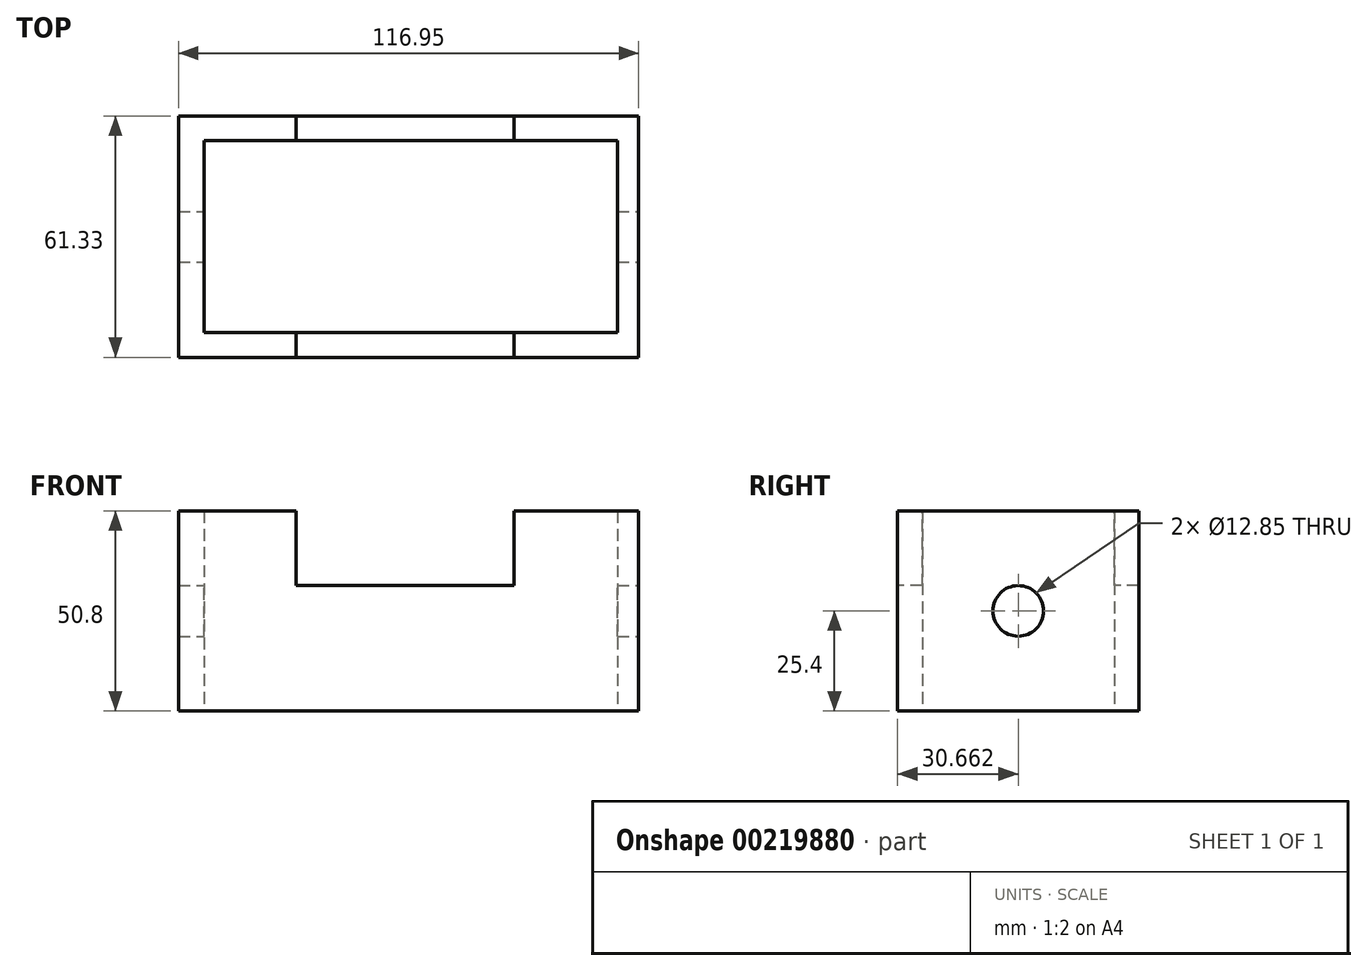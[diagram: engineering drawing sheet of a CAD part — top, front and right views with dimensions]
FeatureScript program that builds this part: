
annotation { "Feature Type Name" : "Feature", "Feature Type Description" : "" }
export const myFeature = defineFeature(function(context is Context, id is Id, definition is map)
    precondition{}
    {
        {
            var Q0;
            Q0=qCreatedBy(makeId("Top.planeOp"),FACE);
            var sketch = newSketch(context, id + "F0", { "sketchPlane" : qUnion([Q0])});
            skLineSegment(sketch, "E0.bottom", {"start": v(-55.34, 27.53) * mm, "end": v(61.61, 27.53) * mm});
            skLineSegment(sketch, "E0.top", {"start": v(-55.34, -33.8) * mm, "end": v(61.61, -33.8) * mm});
            skLineSegment(sketch, "E0.left", {"start": v(-55.34, 27.53) * mm, "end": v(-55.34, -33.8) * mm});
            skLineSegment(sketch, "E0.right", {"start": v(61.61, 27.53) * mm, "end": v(61.61, -33.8) * mm});
            skLineSegment(sketch, "E1.bottom", {"start": v(-48.78, 21.25) * mm, "end": v(56.2, 21.25) * mm});
            skLineSegment(sketch, "E1.top", {"start": v(-48.78, -27.53) * mm, "end": v(56.2, -27.53) * mm});
            skLineSegment(sketch, "E1.left", {"start": v(-48.78, 21.25) * mm, "end": v(-48.78, -27.53) * mm});
            skLineSegment(sketch, "E1.right", {"start": v(56.2, 21.25) * mm, "end": v(56.2, -27.53) * mm});
            skSolve(sketch);
        }
        {
            var Q0;
            Q0 = qSketchRegion(id + "F0", true);
            extrude(context, id + "F1", {"entities" : qUnion([Q0]), "depth" : 50.8 * mm});
        }
        {
            var Q0;
            Q0=makeQuery(id+"F1.opExtrude","SWEPT_FACE",FACE,{"disambiguationData":[OSD([sQuery(id+"F0.wireOp",EDGE,"E0.top")])]});
            var sketch = newSketch(context, id + "F2", { "sketchPlane" : qUnion([Q0])});
            skLineSegment(sketch, "E2", {"start": v(-25.39, 50.8) * mm, "end": v(-25.39, 31.8) * mm});
            skLineSegment(sketch, "E3", {"start": v(-25.39, 31.8) * mm, "end": v(29.95, 31.8) * mm});
            skLineSegment(sketch, "E4", {"start": v(29.95, 31.8) * mm, "end": v(29.95, 50.8) * mm});
            skSolve(sketch);
        }
        {
            var Q0;
            {var subQ0=sQuery(id+"F2.wireOp",EDGE,"E2");Q0=makeQuery(id+"F2.imprint","IMPRINT",FACE,{"disambiguationData":[TD([[makeQuery(id+"F2.imprint","IMPRINT",EDGE,{"derivedFrom":subQ0}),1.0]])]});}
            var Q1;
            Q1=sQuery(id+"F2.wireOp",EDGE,"E4");
            var Q2;
            Q2=sQuery(id+"F2.wireOp",EDGE,"E3");
            var Q3;
            Q3=sQuery(id+"F2.wireOp",EDGE,"E2");
            extrude(context, id + "F3", {"entities" : qUnion([Q0]), "operationType" : NewBodyOperationType.REMOVE, "surfaceEntities" : qUnion([Q1, Q2, Q3]), "oppositeDirection" : true, "depth" : 76.2 * mm});
        }
        {
            var Q0;
            Q0=makeQuery(id+"F1.opExtrude","SWEPT_FACE",FACE,{"disambiguationData":[OSD([sQuery(id+"F0.wireOp",EDGE,"E0.right")])]});
            var sketch = newSketch(context, id + "F4", { "sketchPlane" : qUnion([Q0])});
            skCircle(sketch, "E5", {"center": v(-3.14, 25.4) * mm, "radius": 6.43 * mm});
            skPoint(sketch, "E5.centerSnap0", {"position": v(27.53, 25.4) * mm});
            skPoint(sketch, "E5.centerSnap1", {"position": v(-3.14, 50.8) * mm});
            skSolve(sketch);
        }
        {
            var Q0;
            Q0 = qSketchRegion(id + "F4", true);
            extrude(context, id + "F5", {"entities" : qUnion([Q0]), "operationType" : NewBodyOperationType.REMOVE, "oppositeDirection" : true, "depth" : 177.8 * mm});
        }
    });
